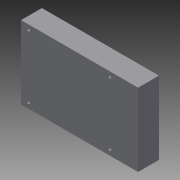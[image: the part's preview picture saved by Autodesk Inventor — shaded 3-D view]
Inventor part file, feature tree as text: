
AUTODESK INVENTOR PART (.ipt)
format: ipt  version: 2013 (Build 170138000, 138)  size: 83,456 bytes
history: native  units: mm
features: extrude x1, sketch x1
ambient origin geometry x8: Origin, YZ Plane, XZ Plane, XY Plane, X Axis, Y Axis, Z Axis, Center Point
bodies: Solid1 (feature_tree)
feature tree (2):
  extrude  "Extrusion1"  Depth=63.0mm
  sketch  "Sketch1"  dims[d0=101.0mm d2=63.0mm d3=3.0mm d4=3.0mm d5=3.0mm d6=3.0mm d9=3.9mm d10=3.9mm d11=6.1mm d12=70.2mm d14=6.1mm d15=70.2mm d16=18.0mm d17=0.0mm d18=54.2mm d19=54.2mm]
